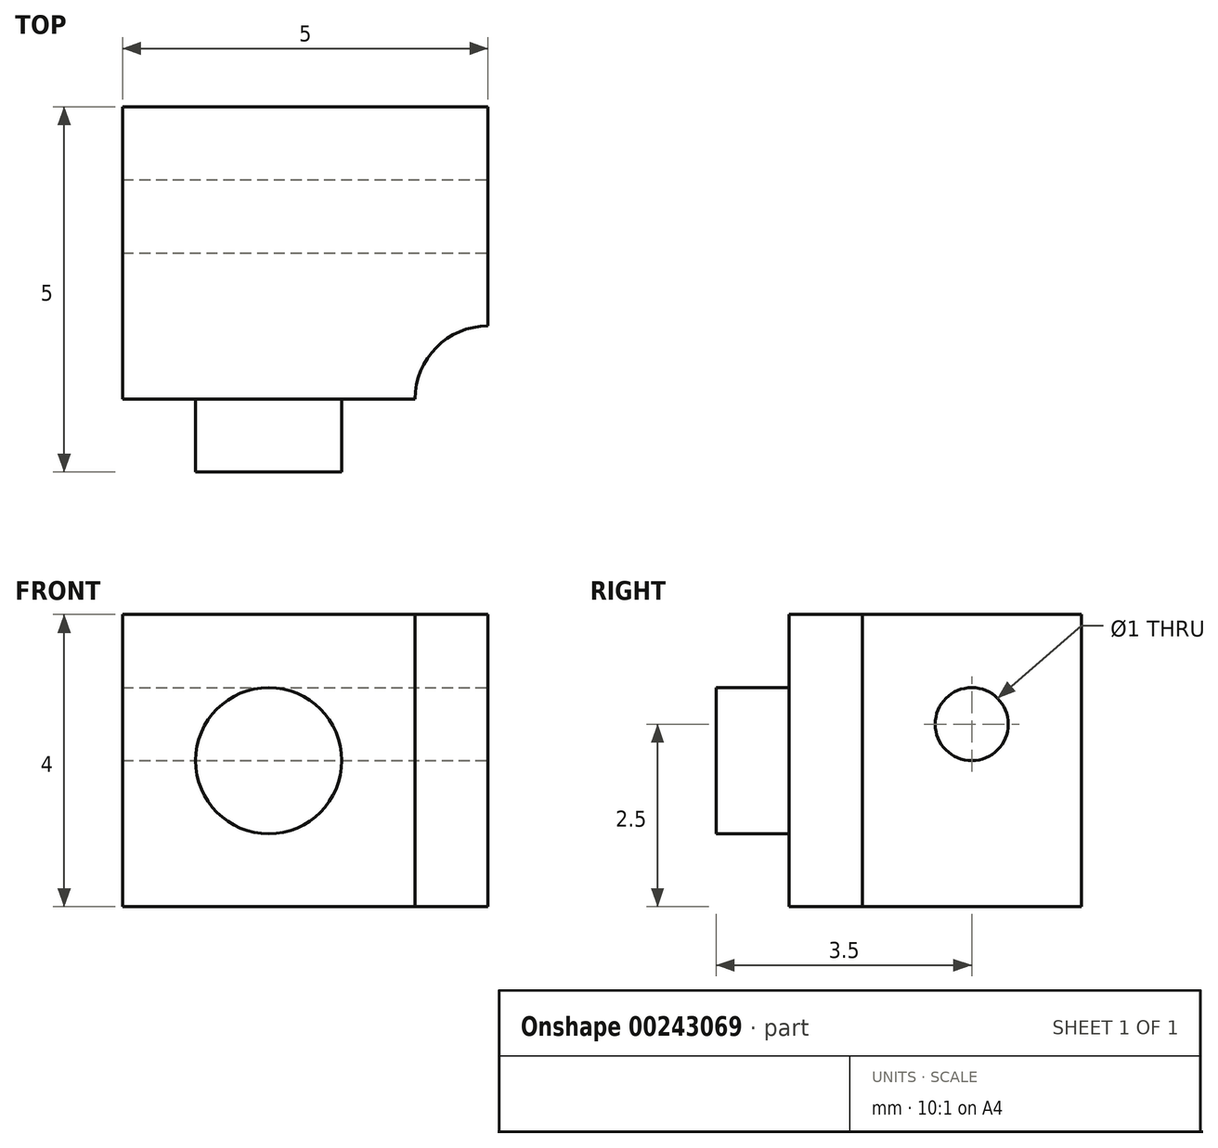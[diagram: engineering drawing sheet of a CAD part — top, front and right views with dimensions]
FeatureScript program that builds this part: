
annotation { "Feature Type Name" : "Feature", "Feature Type Description" : "" }
export const myFeature = defineFeature(function(context is Context, id is Id, definition is map)
    precondition{}
    {
        {
            var Q0;
            Q0=qCreatedBy(makeId("Top.planeOp"),FACE);
            var sketch = newSketch(context, id + "F0", { "sketchPlane" : qUnion([Q0])});
            skLineSegment(sketch, "E0", {"start": v(0, 0) * mm, "end": v(0, 4) * mm});
            skLineSegment(sketch, "E1", {"start": v(0, 4) * mm, "end": v(5, 4) * mm});
            skLineSegment(sketch, "E2", {"start": v(5, 4) * mm, "end": v(5, 1) * mm});
            skLineSegment(sketch, "E3", {"start": v(4, 0) * mm, "end": v(4, 0) * mm});
            skLineSegment(sketch, "E4", {"start": v(4, 0) * mm, "end": v(0, 0) * mm});
            skArc(sketch, "E5", {"start": v(5, 1) * mm, "mid": v(4.3, 0.7) * mm, "end": v(4, 0) * mm});
            skSolve(sketch);
        }
        {
            var Q0;
            Q0=makeQuery(id+"F0.imprint","IMPRINT",FACE,{"disambiguationData":[TD([[makeQuery(id+"F0.imprint","IMPRINT",EDGE,{"derivedFrom":sQuery(id+"F0.wireOp",EDGE,"E0")}),-1.0]])]});
            extrude(context, id + "F1", {"entities" : qUnion([Q0]), "oppositeDirection" : true, "depth" : 4 * mm});
        }
        {
            var Q0;
            Q0=qCreatedBy(makeId("Front.planeOp"),FACE);
            var sketch = newSketch(context, id + "F2", { "sketchPlane" : qUnion([Q0])});
            skLineSegment(sketch, "E6", {"start": v(0, 0) * mm, "end": v(2, 0) * mm, "construction": true});
            skLineSegment(sketch, "E7", {"start": v(2, 0) * mm, "end": v(2, -2) * mm, "construction": true});
            skCircle(sketch, "E8", {"center": v(2, -2) * mm, "radius": 1 * mm});
            skSolve(sketch);
        }
        {
            var Q0;
            Q0 = qSketchRegion(id + "F2", true);
            extrude(context, id + "F3", {"entities" : qUnion([Q0]), "operationType" : NewBodyOperationType.ADD, "depth" : 1 * mm});
        }
        {
            var Q0;
            Q0=makeQuery(id+"F1.opExtrude","SWEPT_FACE",FACE,{"disambiguationData":[OSD([sQuery(id+"F0.wireOp",EDGE,"E2")])]});
            var sketch = newSketch(context, id + "F4", { "sketchPlane" : qUnion([Q0])});
            skLineSegment(sketch, "E9", {"start": v(1, 0) * mm, "end": v(2.5, 0) * mm, "construction": true});
            skLineSegment(sketch, "E10", {"start": v(2.5, 0) * mm, "end": v(2.5, -1.5) * mm, "construction": true});
            skCircle(sketch, "E11", {"center": v(2.5, -1.5) * mm, "radius": 0.5 * mm});
            skSolve(sketch);
        }
        {
            var Q0;
            Q0 = qSketchRegion(id + "F4", true);
            extrude(context, id + "F5", {"entities" : qUnion([Q0]), "operationType" : NewBodyOperationType.REMOVE, "oppositeDirection" : true, "depth" : 25 * mm});
        }
    });
